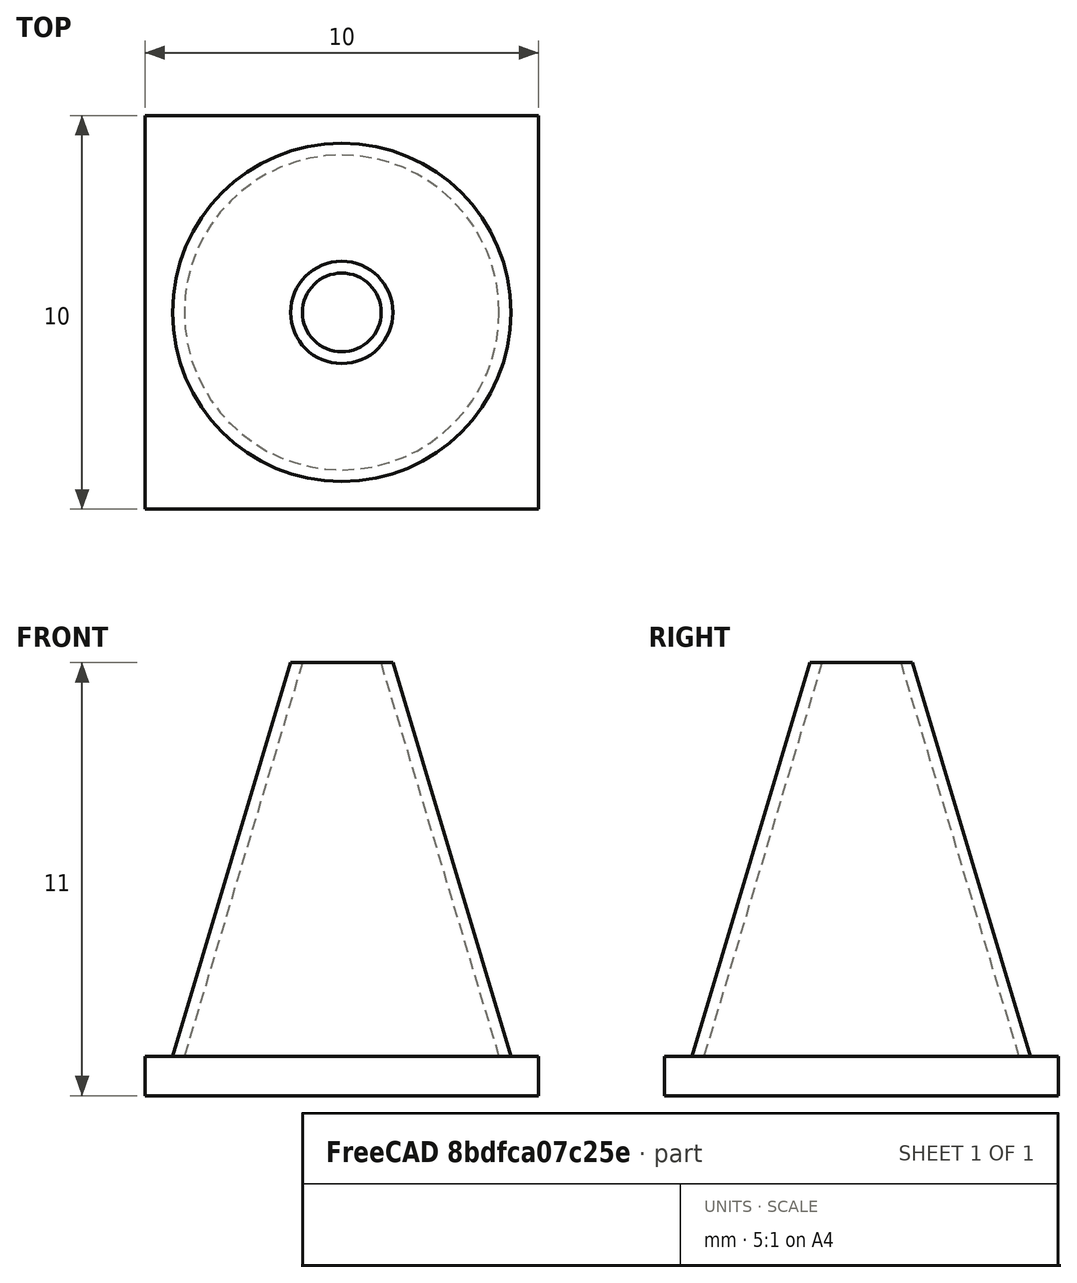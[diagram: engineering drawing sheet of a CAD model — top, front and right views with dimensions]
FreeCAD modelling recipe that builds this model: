
FCSTD DOCUMENT  (FreeCAD 0.21R33694 (Git))
Label: OJT1_T14R02_cono
License: All rights reserved
LicenseURL: http://en.wikipedia.org/wiki/All_rights_reserved
objects: Part::Cone×2, Part::Cut×1, Part::Box×1, Part::MultiFuse×1
note: 5 computed .brp shape members not serialized (recipe doc carries the construction recipe); baked Part::Feature solids carry a one-line shape summary decoded from their .brp

FEATURE [Part::Cone] Cone
  Angle = 360
  AttacherType = Attacher::AttachEngine3D
  Height = 10
  Radius1 = 4
  Radius2 = 1
FEATURE [Part::Cone] Cone001
  Angle = 360
  AttacherType = Attacher::AttachEngine3D
  Height = 10
  Radius1 = 4.3
  Radius2 = 1.3
FEATURE [Part::Cut] Cut
  Base = -> Cone001
  Placement = pos=(0,0,1) rot=(0,0,1;0rad)
  Refine = true
  Tool = -> Cone
FEATURE [Part::Box] Box  label="Cube"
  AttacherType = Attacher::AttachEngine3D
  Height = 1
  Length = 10
  Placement = pos=(-5,-5,0) rot=(0,0,1;0rad)
  Width = 10
FEATURE [Part::MultiFuse] Fusion
  Refine = true
  Shapes = -> [Cut,Box]
